# Revit family: BH1_Surface Wall Mounted Luminaire
name_source: partatom
category: Lighting Fixtures
revit_build: Autodesk Revit MEP 2013 (Build: 20130531_2115(x64)
units: mm (PartAtom-declared; Revit-internal decimal feet)

## types (1)
- 1X18w
    Apparent Load = 18 W
    Body = Whitecroft Lighting_Steel_White_RAL9003
    Color Filter = 16777215
    Dimming Lamp Color Temperature Shift = <None>
    Emit Shape Visible in Rendering = No
    Emit from Circle Diameter = 1000 mm  [stored 3.28084 ft]
    Glass = Glass, Green
    Lamp = 1x18W
    Light Body = Light Body
    Light Source Symbol Length = 3048 mm  [stored 10 ft]
    Load Classification = Ltg
    Material = Bright
    Spot Beam Angle = 30.00°
    Spot Field Angle = 45.00°
    Tilt Angle = 180.00°

note: [stored X ft] marks values corroborated as IEEE doubles in the binary element streams (Revit-internal decimal feet)

## geometry (parser evidence)
native form markers: Blend x6, Sweep x3
no freeform markers — native parametric forms only
